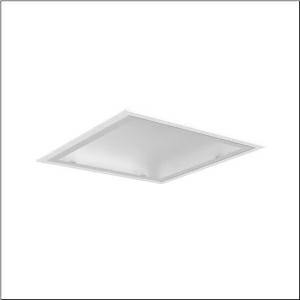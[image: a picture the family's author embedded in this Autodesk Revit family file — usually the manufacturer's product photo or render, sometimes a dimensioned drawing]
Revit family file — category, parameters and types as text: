
# Revit family: mira_11_51fr127a431a
name_source: partatom
category: Lighting Fixtures
units: mm (PartAtom-declared; Revit-internal decimal feet)

## family parameters
Cut with Voids When Loaded = No
Host = Face
Light Source = No
Part Type = Normal
Room Calculation Point = No
Round Connector Dimension = Use Diameter
Shared = No

## types (1)
- Mira 11 (1 x LED, 3060 lm, 23 W, 4000K)
    Apparent Load = 23 VA
    CIE Flux Codes = 51 82 97 100 100
    Color Rendering = 80
    Color Temperature = 4000K
    Default Elevation = 1800 mm
    Description = Mira 11, clean room luminaire, primary light control with reflector, primary optical cover: cover, of toughened safety glass, light emission: direct distribution, primary light characteristic: symmetric, installation type: recessed, LED, rated luminous flux: 3.060lm, luminous efficacy: 133lm/W, light colour: 840, colour temperature: 4000K, control gear: ON/OFF, with terminal, 3-pole, max. 2.5mm², mains connection: 230V, AC, 50/60Hz, rated input power: 23W, luminaire housing, of sheet steel, coated, pure white (RAL 9010), with concealed magnets, module: M625, length: 623mm, width: 623mm, height: 90mm, protection rating (complete): IP65, insulation class (complete): insulation class I (protective earthing), certification: CE, UKCA, permissible operating ambient temperature: -5..+40°C, standard: EN 50419, packaging unit: 1 piece
    Height = 0 mm  [stored 0 ft]
    Lamp = 1 x LED
    Lamp Light Flux = 3060 lm
    Lamp Power = 23 W
    Lamp count = 1
    Length = 625 mm
    Luminous efficacy = 133 lm/W
    Manufacturer = Siteco
    ModVariant = No
    Model = 51FR127A431A
    Mounting Place = Ceiling
    Mounting Type = Recessed
    Number of Poles = 1
    OnlyDefault = Yes
    Power Factor = 1
    Product Name = Mira 11
    Product group = clean room luminaire | ceiling recessed
    ProductGroupID = 402
    Protection Class = Protection class I
    Protection Degree = IP 65
    RLX_Detail_Level = 1
    RLX_Emergency_Light_Flux = 0 lm
    RLX_Emergency_Type = 0
    RLX_Emergency_Type_DB = No
    RlxData = <blob elided: 19285 chars, md5=255a2f21>
    Socket = socket
    Standby Power = 0 W
    System Light Flux = 3060 lm
    System Power = 23 W
    Type Comments = Product without accessories
    Type Image = l_1006636.jpg
    URL = http://relux.com
    VarID = ---
    Voltage = 0 V
    Weight = 0.00 kg
    Width = 625 mm

note: [stored X ft] marks values corroborated as IEEE doubles in the binary element streams (Revit-internal decimal feet)

## geometry (parser evidence)
native form markers: Blend x4, Sweep x10
no freeform markers — native parametric forms only
